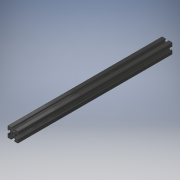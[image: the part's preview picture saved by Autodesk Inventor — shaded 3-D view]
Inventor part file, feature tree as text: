
AUTODESK INVENTOR PART (.ipt)
format: ipt  version: 2019 (Build 230136000, 136)  size: 233,984 bytes
history: native  units: in
note: dims shown in document units (in); Inventor stores cm internally (conversion verified against a paired STEP export)
features: fillet x2, thread x2, extrude x1, sketch x1
ambient origin geometry x8: Origin, YZ Plane, XZ Plane, XY Plane, X Axis, Y Axis, Z Axis, Center Point
bodies: Solid1 (feature_tree)
feature tree (6):
  extrude  "length"  Depth=0.3937in
  fillet  "Fillet1"  Radius=0.1378in
  fillet  "Fillet2"  Radius=0.0394in
  thread  "Thread1"  [1 undecoded]
  thread  "Thread2"  [1 undecoded]
  sketch  "Sketch1"  dims[d0=0.0984in d1=0.3937in d2=0.3937in d3=0.1378in d4=0.0394in d5=90.0deg d6=0.1378in d10=0.0787in d11=0.2749in d13=0.3436in d14=0.0394in d15=1.5748in d17=360.0deg d19=0.1225in d21=5.9055in d22=0.0in d23=0.0071in d24=0.0118in d25=0.315in d26=0.0in d27=0.315in d28=0.0in]
note: 2 required parameter values undecoded (feature->parameter linkage not recoverable at this tier; creation-order binding heuristic only, values carry confidence <= 0.55)
